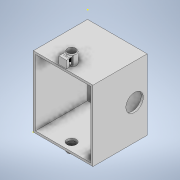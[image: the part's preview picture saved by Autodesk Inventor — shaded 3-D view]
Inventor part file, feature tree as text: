
AUTODESK INVENTOR PART (.ipt)
format: ipt  version: 2020 (Build 240168000, 168)  size: 265,728 bytes
history: native  units: mm
features: sketch x14, extrude x11, fillet x4
ambient origin geometry x8: Origin, YZ Plane, XZ Plane, XY Plane, X Axis, Y Axis, Z Axis, Center Point
bodies: Solid1 (feature_tree)
feature tree (29):
  extrude  "Extrusion1"  Depth=110.0mm
  extrude  "Extrusion2"  Depth=4.0mm
  extrude  "Extrusion3"  Depth=4.0mm
  extrude  "Extrusion4"  Depth=4.0mm TaperAngle=0.0deg
  extrude  "Extrusion5"  Depth=17.0mm
  fillet  "Fillet1"  [1 undecoded]
  fillet  "Fillet2"  Radius=15.0mm
  sketch  "Sketch6"  dims[d16=10.0mm d17=0.0mm d18=20.0mm d19=0.0mm]
  sketch  "Sketch7"  dims[d20=2.0mm d21=2.0mm]
  extrude  "Extrusion6"  Depth=10.0mm TaperAngle=0.0deg
  sketch  "Sketch9"  dims[d28=12.0mm d29=10.0mm d30=0.0mm d31=11.0mm d32=0.0mm d33=6.0mm]
  extrude  "Extrusion7"  Depth=2.0mm
  extrude  "Extrusion8"  Depth=15.5mm
  extrude  "Extrusion9"  Depth=10.0mm TaperAngle=0.0deg
  fillet  "Fillet3"  Radius=11.0mm
  fillet  "Fillet4"  Radius=6.0mm
  extrude  "Extrusion10"  Depth=11.0mm TaperAngle=0.0deg
  extrude  "Extrusion11"  Depth=2.0mm
  sketch  "Sketch1"  dims[d0=130.0mm d1=110.0mm]
  sketch  "Sketch2"  dims[d2=4.0mm d3=4.0mm]
  sketch  "Sketch3"  dims[d4=4.0mm d5=4.0mm]
  sketch  "Sketch4"  dims[d6=100.0mm d7=0.0mm d8=4.0mm d9=0.0mm]
  sketch  "Sketch5"  dims[d10=55.0mm d11=17.0mm d12=0.0mm d13=0.0mm d15=15.0mm]
  sketch  "Sketch8"  dims[d23=17.0mm d27=15.5mm]
  sketch  "Sketch10"  dims[d34=12.2mm d35=11.0mm d36=0.0mm]
  sketch  "Sketch11"  dims[d37=1.0mm d38=0.0mm d39=2.0mm]
  sketch  "Sketch12"  dims[d40=2.0mm]
  sketch  "Sketch13"  dims[d41=0.0mm d42=0.0mm]
  sketch  "Sketch14"  dims[d43=1.0mm d44=0.0mm]
note: 1 required parameter value undecoded (feature->parameter linkage not recoverable at this tier; creation-order binding heuristic only, values carry confidence <= 0.55)
